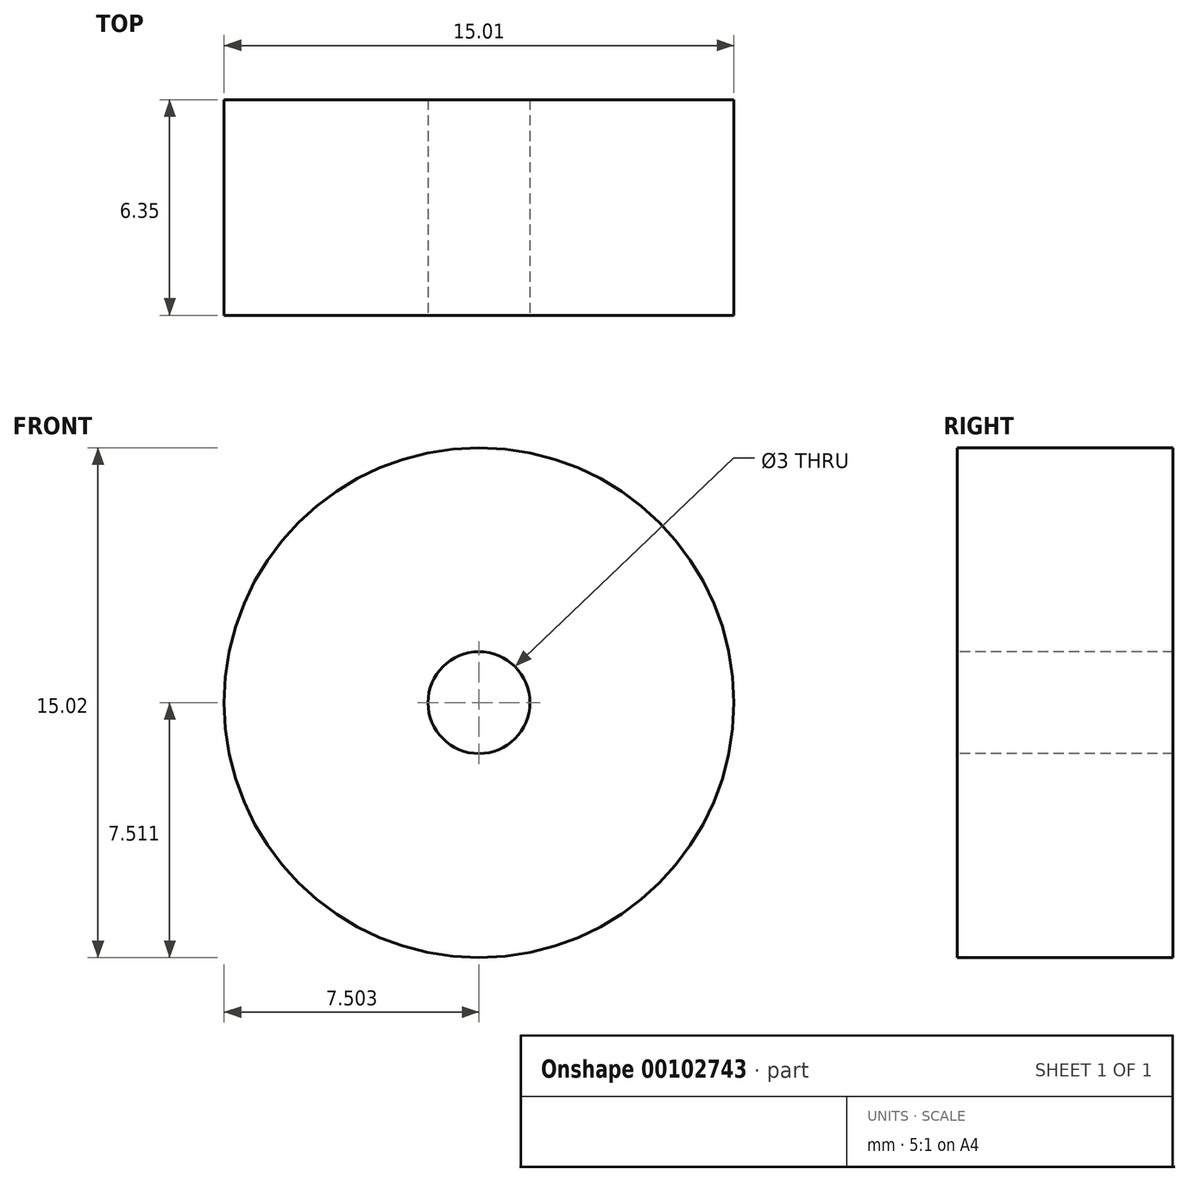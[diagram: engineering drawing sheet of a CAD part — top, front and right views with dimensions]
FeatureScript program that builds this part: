
annotation { "Feature Type Name" : "Feature", "Feature Type Description" : "" }
export const myFeature = defineFeature(function(context is Context, id is Id, definition is map)
    precondition{}
    {
        {
            var Q0;
            Q0=qCreatedBy(makeId("Front.planeOp"),FACE);
            var sketch = newSketch(context, id + "F0", { "sketchPlane" : qUnion([Q0])});
            skCircle(sketch, "E0", {"center": v(-53.98, 27.06) * mm, "radius": 7.5 * mm});
            skSolve(sketch);
        }
        {
            var Q0;
            Q0=makeQuery(id+"F0.imprint","IMPRINT",FACE,{"disambiguationData":[TD([[makeQuery(id+"F0.imprint","IMPRINT",EDGE,{"derivedFrom":sQuery(id+"F0.wireOp",EDGE,"E0")}),1.0]])]});
            extrude(context, id + "F1", {"entities" : qUnion([Q0]), "depth" : 6.35 * mm});
        }
        {
            var Q0;
            Q0=makeQuery(id+"F1.opExtrude","CAP_FACE",FACE,{"disambiguationData":[OSD([sQuery(id+"F0.wireOp",EDGE,"E0")])],"isStart":false});
            var sketch = newSketch(context, id + "F2", { "sketchPlane" : qUnion([Q0])});
            skCircle(sketch, "E1", {"center": v(-53.98, 27.06) * mm, "radius": 1.5 * mm});
            skSolve(sketch);
        }
        {
            var Q0;
            Q0 = qSketchRegion(id + "F2", true);
            extrude(context, id + "F3", {"entities" : qUnion([Q0]), "operationType" : NewBodyOperationType.REMOVE, "endBound" : BoundingType.THROUGH_ALL, "oppositeDirection" : true, "depth" : 25.4 * mm});
        }
    });
